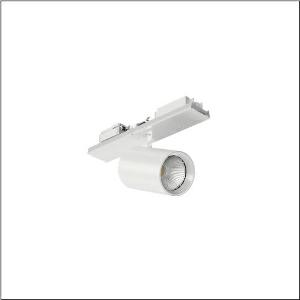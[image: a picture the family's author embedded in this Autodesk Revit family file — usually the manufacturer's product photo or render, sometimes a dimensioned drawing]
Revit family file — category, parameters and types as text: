
# Revit family: licross_r__spot_31_51sl137a43b_0799
name_source: partatom
category: Lighting Fixtures
units: mm (PartAtom-declared; Revit-internal decimal feet)

## family parameters
Cut with Voids When Loaded = No
Host = Face
Light Source = No
Part Type = Normal
Room Calculation Point = No
Round Connector Dimension = Use Diameter
Shared = No

## types (1)
- --- (1 x LED, 3680 lm, 28 W, 4000K)
    Apparent Load = 28 VA
    CIE Flux Codes = 92 97 99 100 100
    Color Rendering = 90
    Color Temperature = 4000K
    Default Elevation = 1800 mm
    Description = Licross® Spot 31, directional spotlight, light control with lens, of plastic, LED rated luminous flux: 3.680lm, light colour: 940, with plug, 3-pole, with phase selection, mains connection: 220..240V, AC, 50/60Hz, of aluminium, traffic white (RAL 9016), length: 140mm, diameter: 90mm, protection rating (complete): IP20, insulation class (complete): insulation class I (protective earthing), certification: CE, packaging unit: 1 piece
    Height = 175 mm
    Lamp = 1 x LED
    Lamp Light Flux = 3680 lm
    Lamp Power = 28 W
    Lamp count = 1
    Length = 90 mm
    Luminous efficacy = 131 lm/W
    Manufacturer = Siteco
    ModVariant = No
    Model = 51SL137A43B
    Mounting Place = Ceiling
    Mounting Type = Pendant
    Number of Poles = 1
    OnlyDefault = Yes
    Power Factor = 1
    Product Name = Licross® Spot 31
    Product group = directional spotlight
    ProductGroupID = 905
    Protection Class = Protection class I
    Protection Degree = IP 20
    RLX_Detail_Level = 1
    RLX_Emergency_Light_Flux = 0 lm
    RLX_Emergency_Type = 0
    RLX_Emergency_Type_DB = No
    RlxData = <blob elided: 14893 chars, md5=8fb7c0ce>
    Socket = socket
    Standby Power = 0 W
    System Light Flux = 3680 lm
    System Power = 28 W
    Type Comments = factory setting: luminous flux: 100 % | (ON | ON | ON) | 700 mA
    Type Image = l_1245720.jpg
    URL = http://relux.com
    VarID = @adj_081971
    Voltage = 0 V
    Weight = 0.00 kg
    Width = 0 mm  [stored 0 ft]

note: [stored X ft] marks values corroborated as IEEE doubles in the binary element streams (Revit-internal decimal feet)

## geometry (parser evidence)
native form markers: Sweep x12
no freeform markers — native parametric forms only
